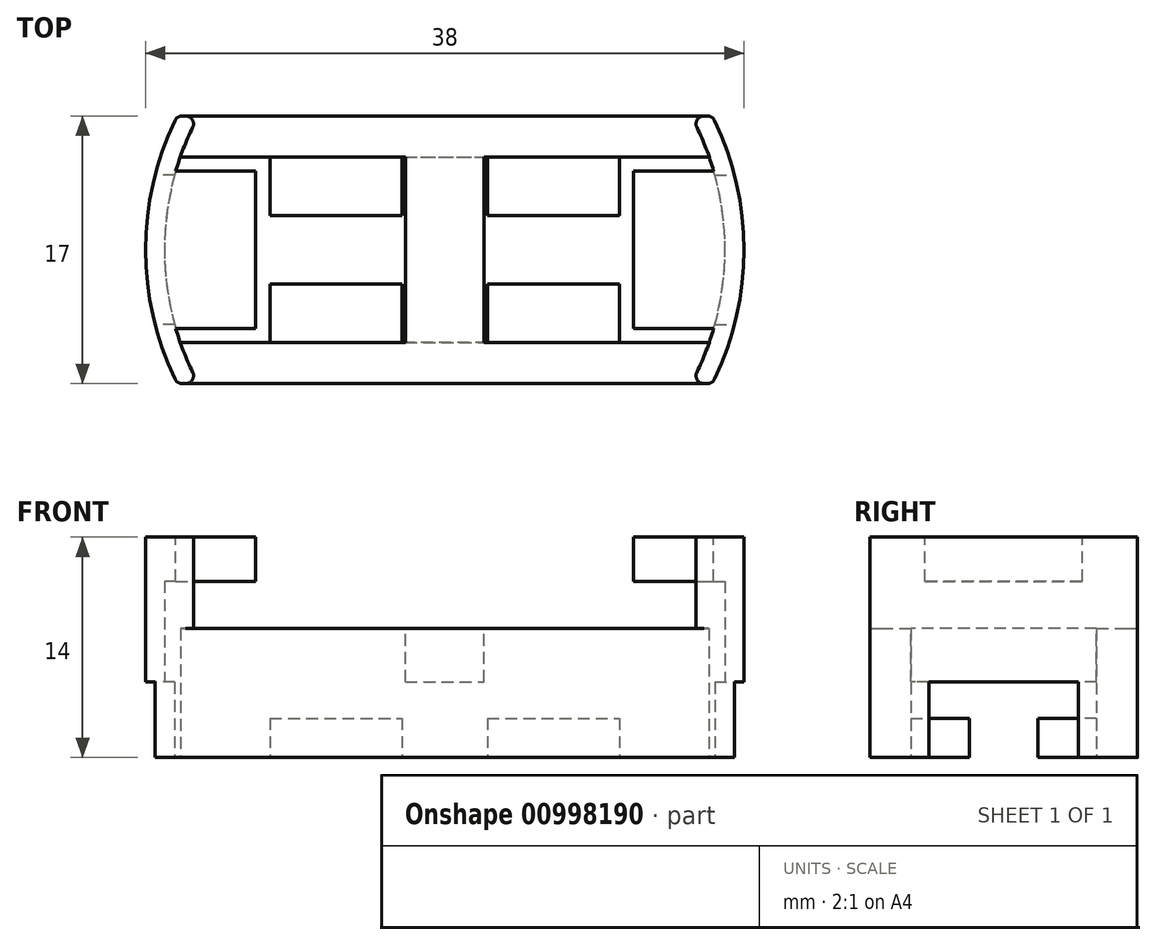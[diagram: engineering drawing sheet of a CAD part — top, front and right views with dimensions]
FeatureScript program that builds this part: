
annotation { "Feature Type Name" : "Feature", "Feature Type Description" : "" }
export const myFeature = defineFeature(function(context is Context, id is Id, definition is map)
    precondition{}
    {
        {
            var Q0;
            Q0=qCreatedBy(makeId("Top.planeOp"),FACE);
            var sketch = newSketch(context, id + "F0", { "sketchPlane" : qUnion([Q0])});
            skArc(sketch, "E0", {"start": v(17, -8.5) * mm, "mid": v(19, 0) * mm, "end": v(17, 8.5) * mm});
            skLineSegment(sketch, "E1.bottom", {"start": v(-17, 8.5) * mm, "end": v(17, 8.5) * mm});
            skLineSegment(sketch, "E1.top", {"start": v(-17, -8.5) * mm, "end": v(17, -8.5) * mm});
            skArc(sketch, "E2.trimOffspring", {"start": v(-17, 8.5) * mm, "mid": v(-19, 0) * mm, "end": v(-17, -8.5) * mm});
            skSolve(sketch);
        }
        {
            var Q0;
            Q0=makeQuery(id+"F0.imprint","IMPRINT",FACE,{"disambiguationData":[TD([[makeQuery(id+"F0.imprint","IMPRINT",EDGE,{"derivedFrom":sQuery(id+"F0.wireOp",EDGE,"E0")}),1.0]])]});
            extrude(context, id + "F1", {"entities" : qUnion([Q0]), "depth" : 14 * mm, "offsetDistance" : 25 * mm});
        }
        {
            var Q0;
            Q0=makeQuery(id+"F1.opExtrude","SWEPT_FACE",FACE,{"disambiguationData":[OSD([sQuery(id+"F0.wireOp",EDGE,"E1.top")])]});
            var sketch = newSketch(context, id + "F2", { "sketchPlane" : qUnion([Q0])});
            skLineSegment(sketch, "E3.bottom", {"start": v(-12, 14) * mm, "end": v(12, 14) * mm});
            skLineSegment(sketch, "E3.top", {"start": v(-12, 8.2) * mm, "end": v(12, 8.2) * mm});
            skLineSegment(sketch, "E3.left", {"start": v(-12, 14) * mm, "end": v(-12, 8.2) * mm});
            skLineSegment(sketch, "E3.right", {"start": v(12, 14) * mm, "end": v(12, 8.2) * mm});
            skSolve(sketch);
        }
        {
            var Q0;
            Q0=makeQuery(id+"F2.imprint","IMPRINT",FACE,{"disambiguationData":[TD([[makeQuery(id+"F2.imprint","IMPRINT",EDGE,{"derivedFrom":sQuery(id+"F2.wireOp",EDGE,"E3.bottom")}),-1.0]])]});
            extrude(context, id + "F3", {"entities" : qUnion([Q0]), "operationType" : NewBodyOperationType.REMOVE, "oppositeDirection" : true, "depth" : 25 * mm, "offsetDistance" : 25 * mm});
        }
        {
            var Q0;
            Q0=makeQuery(id+"F3.boolean.opBoolean","COPY",FACE,{"derivedFrom":makeQuery(id+"F3.opExtrude","SWEPT_FACE",FACE,{"disambiguationData":[OSD([sQuery(id+"F2.wireOp",EDGE,"E3.top")])]})});
            var sketch = newSketch(context, id + "F4", { "sketchPlane" : qUnion([Q0])});
            skCircle(sketch, "E4", {"center": v(0, 0) * mm, "radius": 17.8 * mm});
            skSolve(sketch);
        }
        {
            var Q0;
            Q0=makeQuery(id+"F4.imprint","IMPRINT",FACE,{"disambiguationData":[TD([[makeQuery(id+"F4.imprint","IMPRINT",EDGE,{"derivedFrom":sQuery(id+"F4.wireOp",EDGE,"E4")}),1.0]])]});
            extrude(context, id + "F5", {"entities" : qUnion([Q0]), "operationType" : NewBodyOperationType.REMOVE, "depth" : 3 * mm, "offsetDistance" : 25 * mm});
        }
        {
            var Q0;
            {var subQ0=sQuery(id+"F0.wireOp",EDGE,"E0");var subQ1=sQuery(id+"F0.wireOp",EDGE,"E1.bottom");var subQ2=sQuery(id+"F0.wireOp",EDGE,"E1.top");Q0=makeQuery(id+"F3.boolean.opBoolean","SPLIT",FACE,{"disambiguationData":[TD([makeQuery(id+"F1.opExtrude","SWEPT_FACE",FACE,{"disambiguationData":[OSD([subQ0])]})])],"derivedFrom":makeQuery(id+"F1.opExtrude","CAP_FACE",FACE,{"disambiguationData":[OSD([subQ0,subQ1,subQ2,sQuery(id+"F0.wireOp",EDGE,"E2.trimOffspring")])],"isStart":false})});}
            var sketch = newSketch(context, id + "F6", { "sketchPlane" : qUnion([Q0])});
            skArc(sketch, "E5", {"start": v(17.08, 5) * mm, "mid": v(0, 17.8) * mm, "end": v(-17.08, 5) * mm});
            skLineSegment(sketch, "E6.bottom", {"start": v(-17.08, 5) * mm, "end": v(17.08, 5) * mm});
            skLineSegment(sketch, "E6.top", {"start": v(-17.08, -5) * mm, "end": v(17.08, -5) * mm});
            skPoint(sketch, "E6.right.end.orphan", {"position": v(23.45, -5) * mm});
            skArc(sketch, "E7.trimOffspring", {"start": v(-17.08, -5) * mm, "mid": v(0, -17.8) * mm, "end": v(17.08, -5) * mm});
            skSolve(sketch);
        }
        {
            var Q0;
            {var subQ0=sQuery(id+"F6.wireOp",EDGE,"E6.bottom");var subQ1=sQuery(id+"F6.wireOp",EDGE,"E5");var subQ2=makeQuery(id+"F6.imprint","INTERSECT",VERTEX,{"disambiguationData":[OD(1.0)],"derivedFrom":[subQ1,subQ0]});Q0=makeQuery(id+"F6.imprint","IMPRINT",FACE,{"disambiguationData":[TD([[makeQuery(id+"F6.imprint","IMPRINT",EDGE,{"disambiguationData":[TD([[subQ2,-1.0]])],"derivedFrom":subQ0}),1.0]])]});}
            var Q1;
            {var subQ0=sQuery(id+"F6.wireOp",EDGE,"E7.trimOffspring");var subQ1=sQuery(id+"F6.wireOp",EDGE,"E6.top");var subQ2=makeQuery(id+"F6.imprint","INTERSECT",VERTEX,{"disambiguationData":[OD(0.0)],"derivedFrom":[subQ1,subQ0]});Q1=makeQuery(id+"F6.imprint","IMPRINT",FACE,{"disambiguationData":[TD([[makeQuery(id+"F6.imprint","IMPRINT",EDGE,{"disambiguationData":[TD([[subQ2,-1.0]])],"derivedFrom":subQ1}),-1.0]])]});}
            var Q2;
            {var subQ0=sQuery(id+"F6.wireOp",EDGE,"E6.bottom");var subQ1=sQuery(id+"F6.wireOp",EDGE,"E5");var subQ2=makeQuery(id+"F6.imprint","INTERSECT",VERTEX,{"disambiguationData":[OD(0.0)],"derivedFrom":[subQ1,subQ0]});Q2=makeQuery(id+"F6.imprint","IMPRINT",FACE,{"disambiguationData":[TD([[makeQuery(id+"F6.imprint","IMPRINT",EDGE,{"disambiguationData":[TD([[subQ2,1.0]])],"derivedFrom":subQ0}),1.0]])]});}
            var Q3;
            {var subQ0=sQuery(id+"F6.wireOp",EDGE,"E7.trimOffspring");var subQ1=sQuery(id+"F6.wireOp",EDGE,"E6.top");var subQ2=makeQuery(id+"F6.imprint","INTERSECT",VERTEX,{"disambiguationData":[OD(1.0)],"derivedFrom":[subQ1,subQ0]});Q3=makeQuery(id+"F6.imprint","IMPRINT",FACE,{"disambiguationData":[TD([[makeQuery(id+"F6.imprint","IMPRINT",EDGE,{"disambiguationData":[TD([[subQ2,1.0]])],"derivedFrom":subQ1}),-1.0]])]});}
            extrude(context, id + "F7", {"entities" : qUnion([Q0, Q1, Q2, Q3]), "operationType" : NewBodyOperationType.REMOVE, "oppositeDirection" : true, "depth" : 4 * mm, "offsetDistance" : 25 * mm});
        }
        {
            var Q0;
            Q0=makeQuery(id+"F1.opExtrude","CAP_FACE",FACE,{"disambiguationData":[OSD([sQuery(id+"F0.wireOp",EDGE,"E0"),sQuery(id+"F0.wireOp",EDGE,"E1.bottom"),sQuery(id+"F0.wireOp",EDGE,"E1.top"),sQuery(id+"F0.wireOp",EDGE,"E2.trimOffspring")])],"isStart":true});
            var sketch = newSketch(context, id + "F8", { "sketchPlane" : qUnion([Q0])});
            skLineSegment(sketch, "E8.top", {"start": v(-16.8, -5.9) * mm, "end": v(16.8, -5.9) * mm});
            skLineSegment(sketch, "E9", {"start": v(0, 0) * mm, "end": v(0, -2.2) * mm});
            skArc(sketch, "E10", {"start": v(-16.8, 5.9) * mm, "mid": v(-17.8, 0) * mm, "end": v(-16.8, -5.9) * mm});
            skLineSegment(sketch, "E11", {"start": v(16.8, 5.9) * mm, "end": v(-16.8, 5.9) * mm});
            skArc(sketch, "E12.trimOffspring", {"start": v(16.8, -5.9) * mm, "mid": v(17.8, 0) * mm, "end": v(16.8, 5.9) * mm});
            skSolve(sketch);
        }
        {
            var Q0;
            Q0 = qSketchRegion(id + "F8", true);
            extrude(context, id + "F9", {"entities" : qUnion([Q0]), "operationType" : NewBodyOperationType.REMOVE, "oppositeDirection" : true, "depth" : 9 * mm, "offsetDistance" : 25 * mm});
        }
        {
            var Q0;
            {var subQ0=sQuery(id+"F4.wireOp",EDGE,"E4");var subQ2=sQuery(id+"F0.wireOp",EDGE,"E1.bottom");var subQ3=sQuery(id+"F2.wireOp",EDGE,"E3.top");Q0=makeQuery(id+"F9.boolean.opBoolean","SPLIT",FACE,{"disambiguationData":[TD([makeQuery(id+"F1.opExtrude","SWEPT_FACE",FACE,{"disambiguationData":[OSD([subQ2])]})])],"derivedFrom":makeQuery(id+"F5.boolean.opBoolean","MERGE",FACE,{"derivedFrom":[makeQuery(id+"F3.boolean.opBoolean","COPY",FACE,{"derivedFrom":makeQuery(id+"F3.opExtrude","SWEPT_FACE",FACE,{"disambiguationData":[OSD([subQ3])]})})],"fromTools":[makeQuery(id+"F5.opExtrude","CAP_FACE",FACE,{"disambiguationData":[OSD([subQ2,subQ3,sQuery(id+"F2.wireOp",EDGE,"E3.left"),sQuery(id+"F2.wireOp",EDGE,"E3.right"),subQ0])],"isStart":true})]})});}
            var sketch = newSketch(context, id + "F10", { "sketchPlane" : qUnion([Q0])});
            skLineSegment(sketch, "E13.bottom", {"start": v(-2.5, 5.9) * mm, "end": v(2.5, 5.9) * mm});
            skLineSegment(sketch, "E13.top", {"start": v(-2.5, -5.9) * mm, "end": v(2.5, -5.9) * mm});
            skLineSegment(sketch, "E13.left", {"start": v(-2.5, 5.9) * mm, "end": v(-2.5, -5.9) * mm});
            skLineSegment(sketch, "E13.right", {"start": v(2.5, 5.9) * mm, "end": v(2.5, -5.9) * mm});
            skSolve(sketch);
        }
        {
            var Q0;
            Q0=makeQuery(id+"F10.imprint","IMPRINT",FACE,{"disambiguationData":[TD([[makeQuery(id+"F10.imprint","IMPRINT",EDGE,{"derivedFrom":sQuery(id+"F10.wireOp",EDGE,"E13.bottom")}),-1.0]])]});
            extrude(context, id + "F11", {"entities" : qUnion([Q0]), "operationType" : NewBodyOperationType.ADD, "oppositeDirection" : true, "depth" : (8.2 - 4.8) * mm, "offsetDistance" : 25 * mm});
        }
        {
            var Q0;
            Q0=makeQuery(id+"F1.opExtrude","CAP_FACE",FACE,{"disambiguationData":[OSD([sQuery(id+"F0.wireOp",EDGE,"E0"),sQuery(id+"F0.wireOp",EDGE,"E1.bottom"),sQuery(id+"F0.wireOp",EDGE,"E1.top"),sQuery(id+"F0.wireOp",EDGE,"E2.trimOffspring")])],"isStart":true});
            var sketch = newSketch(context, id + "F12", { "sketchPlane" : qUnion([Q0])});
            skLineSegment(sketch, "E14.bottom", {"start": v(-11.1, 5.9) * mm, "end": v(-2.7, 5.9) * mm});
            skLineSegment(sketch, "E14.top", {"start": v(-11.1, 2.17) * mm, "end": v(-2.7, 2.17) * mm});
            skLineSegment(sketch, "E14.left", {"start": v(-11.1, 5.9) * mm, "end": v(-11.1, 2.17) * mm});
            skLineSegment(sketch, "E14.right", {"start": v(-2.7, 5.9) * mm, "end": v(-2.7, 2.17) * mm});
            skLineSegment(sketch, "E15", {"start": v(0, 0) * mm, "end": v(-2, 0) * mm});
            skLineSegment(sketch, "E16", {"start": v(0, 0) * mm, "end": v(0, 1.7) * mm});
            skLineSegment(sketch, "E17.MirrorCS", {"start": v(-11.1, -2.17) * mm, "end": v(-2.7, -2.17) * mm});
            skLineSegment(sketch, "E18.MirrorCS", {"start": v(-11.1, -5.9) * mm, "end": v(-2.7, -5.9) * mm});
            skLineSegment(sketch, "E19.MirrorCS", {"start": v(-2.7, -5.9) * mm, "end": v(-2.7, -2.17) * mm});
            skLineSegment(sketch, "E20.MirrorCS", {"start": v(-11.1, -5.9) * mm, "end": v(-11.1, -2.17) * mm});
            skLineSegment(sketch, "E21.MirrorCS", {"start": v(2.7, 5.9) * mm, "end": v(2.7, 2.17) * mm});
            skLineSegment(sketch, "E22.MirrorCS", {"start": v(11.1, -5.9) * mm, "end": v(11.1, -2.17) * mm});
            skLineSegment(sketch, "E23.MirrorCS", {"start": v(11.1, 5.9) * mm, "end": v(11.1, 2.17) * mm});
            skLineSegment(sketch, "E24.MirrorCS", {"start": v(11.1, -2.17) * mm, "end": v(2.7, -2.17) * mm});
            skLineSegment(sketch, "E25.MirrorCS", {"start": v(11.1, 5.9) * mm, "end": v(2.7, 5.9) * mm});
            skLineSegment(sketch, "E26.MirrorCS", {"start": v(2.7, -5.9) * mm, "end": v(2.7, -2.17) * mm});
            skLineSegment(sketch, "E27.MirrorCS", {"start": v(11.1, -5.9) * mm, "end": v(2.7, -5.9) * mm});
            skLineSegment(sketch, "E28.MirrorCS", {"start": v(11.1, 2.17) * mm, "end": v(2.7, 2.17) * mm});
            skSolve(sketch);
        }
        {
            var Q0;
            Q0 = qSketchRegion(id + "F12", true);
            extrude(context, id + "F13", {"entities" : qUnion([Q0]), "operationType" : NewBodyOperationType.ADD, "oppositeDirection" : true, "depth" : (8.2 - 5.7) * mm, "offsetDistance" : 25 * mm});
        }
        {
            var Q0;
            Q0=makeQuery(id+"F13.boolean.opBoolean","MERGE",FACE,{"derivedFrom":[makeQuery(id+"F1.opExtrude","CAP_FACE",FACE,{"disambiguationData":[OSD([sQuery(id+"F0.wireOp",EDGE,"E0"),sQuery(id+"F0.wireOp",EDGE,"E1.bottom"),sQuery(id+"F0.wireOp",EDGE,"E1.top"),sQuery(id+"F0.wireOp",EDGE,"E2.trimOffspring")])],"isStart":true}),makeQuery(id+"F13.opExtrude","CAP_FACE",FACE,{"disambiguationData":[OSD([sQuery(id+"F12.wireOp",EDGE,"E17.MirrorCS"),sQuery(id+"F12.wireOp",EDGE,"E18.MirrorCS"),sQuery(id+"F12.wireOp",EDGE,"E19.MirrorCS"),sQuery(id+"F12.wireOp",EDGE,"E20.MirrorCS")])],"isStart":true}),makeQuery(id+"F13.opExtrude","CAP_FACE",FACE,{"disambiguationData":[OSD([sQuery(id+"F12.wireOp",EDGE,"E14.bottom"),sQuery(id+"F12.wireOp",EDGE,"E14.right"),sQuery(id+"F12.wireOp",EDGE,"E14.top"),sQuery(id+"F12.wireOp",EDGE,"E14.left")])],"isStart":true}),makeQuery(id+"F13.opExtrude","CAP_FACE",FACE,{"disambiguationData":[OSD([sQuery(id+"F12.wireOp",EDGE,"E25.MirrorCS"),sQuery(id+"F12.wireOp",EDGE,"E21.MirrorCS"),sQuery(id+"F12.wireOp",EDGE,"E23.MirrorCS"),sQuery(id+"F12.wireOp",EDGE,"E28.MirrorCS")])],"isStart":true}),makeQuery(id+"F13.opExtrude","CAP_FACE",FACE,{"disambiguationData":[OSD([sQuery(id+"F12.wireOp",EDGE,"E26.MirrorCS"),sQuery(id+"F12.wireOp",EDGE,"E24.MirrorCS"),sQuery(id+"F12.wireOp",EDGE,"E22.MirrorCS"),sQuery(id+"F12.wireOp",EDGE,"E27.MirrorCS")])],"isStart":true})]});
            var sketch = newSketch(context, id + "F14", { "sketchPlane" : qUnion([Q0])});
            skLineSegment(sketch, "E29.bottom", {"start": v(-12, 4.75) * mm, "end": v(-24, 4.75) * mm});
            skLineSegment(sketch, "E29.top", {"start": v(-12, -4.75) * mm, "end": v(-24, -4.75) * mm});
            skLineSegment(sketch, "E29.left", {"start": v(-12, 4.75) * mm, "end": v(-12, -4.75) * mm});
            skLineSegment(sketch, "E29.right", {"start": v(-24, 4.75) * mm, "end": v(-24, -4.75) * mm});
            skLineSegment(sketch, "E30", {"start": v(0, 0) * mm, "end": v(0, 4.03) * mm});
            skLineSegment(sketch, "E31.MirrorCS", {"start": v(12, 4.75) * mm, "end": v(12, -4.75) * mm});
            skLineSegment(sketch, "E32.MirrorCS", {"start": v(12, 4.75) * mm, "end": v(24, 4.75) * mm});
            skLineSegment(sketch, "E33.MirrorCS", {"start": v(12, -4.75) * mm, "end": v(24, -4.75) * mm});
            skLineSegment(sketch, "E34.MirrorCS", {"start": v(24, 4.75) * mm, "end": v(24, -4.75) * mm});
            skSolve(sketch);
        }
        {
            var Q0;
            Q0 = qSketchRegion(id + "F14", true);
            extrude(context, id + "F15", {"entities" : qUnion([Q0]), "operationType" : NewBodyOperationType.REMOVE, "oppositeDirection" : true, "depth" : (14 - 9.2) * mm, "offsetDistance" : 25 * mm});
        }
        {
            var Q0;
            Q0=makeQuery(id+"F1.opExtrude","SWEPT_EDGE",EDGE,{"disambiguationData":[OSD([sQuery(id+"F0.wireOp",EDGE,"E1.top"),sQuery(id+"F0.wireOp",EDGE,"E2.trimOffspring")])]});
            var Q1;
            Q1=makeQuery(id+"F1.opExtrude","SWEPT_EDGE",EDGE,{"disambiguationData":[OSD([sQuery(id+"F0.wireOp",EDGE,"E0"),sQuery(id+"F0.wireOp",EDGE,"E1.top")])]});
            var Q2;
            Q2=makeQuery(id+"F1.opExtrude","SWEPT_EDGE",EDGE,{"disambiguationData":[OSD([sQuery(id+"F0.wireOp",EDGE,"E0"),sQuery(id+"F0.wireOp",EDGE,"E1.bottom")])]});
            var Q3;
            Q3=makeQuery(id+"F1.opExtrude","SWEPT_EDGE",EDGE,{"disambiguationData":[OSD([sQuery(id+"F0.wireOp",EDGE,"E1.bottom"),sQuery(id+"F0.wireOp",EDGE,"E2.trimOffspring")])]});
            var Q4;
            {var subQ0=makeQuery(id+"F1.opExtrude","SWEPT_FACE",FACE,{"disambiguationData":[OSD([sQuery(id+"F0.wireOp",EDGE,"E1.top")])]});var subQ1=makeQuery(id+"F7.opExtrude","SWEPT_FACE",FACE,{"disambiguationData":[OSD([sQuery(id+"F6.wireOp",EDGE,"E7.trimOffspring")])]});Q4=makeQuery(id+"F7.boolean.opBoolean","INTERSECT",EDGE,{"disambiguationData":[topologyDisambiguationEdgeConnected([makeQuery(id+"F5.boolean.opBoolean","COPY",FACE,{"disambiguationData":[OD(0.0)],"derivedFrom":makeQuery(id+"F5.opExtrude","SWEPT_FACE",FACE,{"disambiguationData":[OSD([sQuery(id+"F4.wireOp",EDGE,"E4")])]})})])],"derivedFrom":[subQ0,subQ1]});}
            var Q5;
            {var subQ0=makeQuery(id+"F1.opExtrude","SWEPT_FACE",FACE,{"disambiguationData":[OSD([sQuery(id+"F0.wireOp",EDGE,"E1.bottom")])]});var subQ1=makeQuery(id+"F7.opExtrude","SWEPT_FACE",FACE,{"disambiguationData":[OSD([sQuery(id+"F6.wireOp",EDGE,"E5")])]});Q5=makeQuery(id+"F7.boolean.opBoolean","INTERSECT",EDGE,{"disambiguationData":[topologyDisambiguationEdgeConnected([makeQuery(id+"F5.boolean.opBoolean","COPY",FACE,{"disambiguationData":[OD(0.0)],"derivedFrom":makeQuery(id+"F5.opExtrude","SWEPT_FACE",FACE,{"disambiguationData":[OSD([sQuery(id+"F4.wireOp",EDGE,"E4")])]})})])],"derivedFrom":[subQ0,subQ1]});}
            var Q6;
            {var subQ0=makeQuery(id+"F1.opExtrude","SWEPT_FACE",FACE,{"disambiguationData":[OSD([sQuery(id+"F0.wireOp",EDGE,"E1.top")])]});var subQ1=makeQuery(id+"F7.opExtrude","SWEPT_FACE",FACE,{"disambiguationData":[OSD([sQuery(id+"F6.wireOp",EDGE,"E7.trimOffspring")])]});Q6=makeQuery(id+"F7.boolean.opBoolean","INTERSECT",EDGE,{"disambiguationData":[topologyDisambiguationEdgeConnected([makeQuery(id+"F5.boolean.opBoolean","COPY",FACE,{"disambiguationData":[OD(1.0)],"derivedFrom":makeQuery(id+"F5.opExtrude","SWEPT_FACE",FACE,{"disambiguationData":[OSD([sQuery(id+"F4.wireOp",EDGE,"E4")])]})})])],"derivedFrom":[subQ0,subQ1]});}
            var Q7;
            {var subQ0=makeQuery(id+"F1.opExtrude","SWEPT_FACE",FACE,{"disambiguationData":[OSD([sQuery(id+"F0.wireOp",EDGE,"E1.bottom")])]});var subQ1=makeQuery(id+"F7.opExtrude","SWEPT_FACE",FACE,{"disambiguationData":[OSD([sQuery(id+"F6.wireOp",EDGE,"E5")])]});Q7=makeQuery(id+"F7.boolean.opBoolean","INTERSECT",EDGE,{"disambiguationData":[topologyDisambiguationEdgeConnected([makeQuery(id+"F5.boolean.opBoolean","COPY",FACE,{"disambiguationData":[OD(1.0)],"derivedFrom":makeQuery(id+"F5.opExtrude","SWEPT_FACE",FACE,{"disambiguationData":[OSD([sQuery(id+"F4.wireOp",EDGE,"E4")])]})})])],"derivedFrom":[subQ0,subQ1]});}
            fillet(context, id + "F16", {"entities" : qUnion([Q0, Q1, Q2, Q3, Q4, Q5, Q6, Q7]), "radius" : 0.5 * mm, "tangentPropagation" : true, "allowEdgeOverflow" : false});
        }
    });
